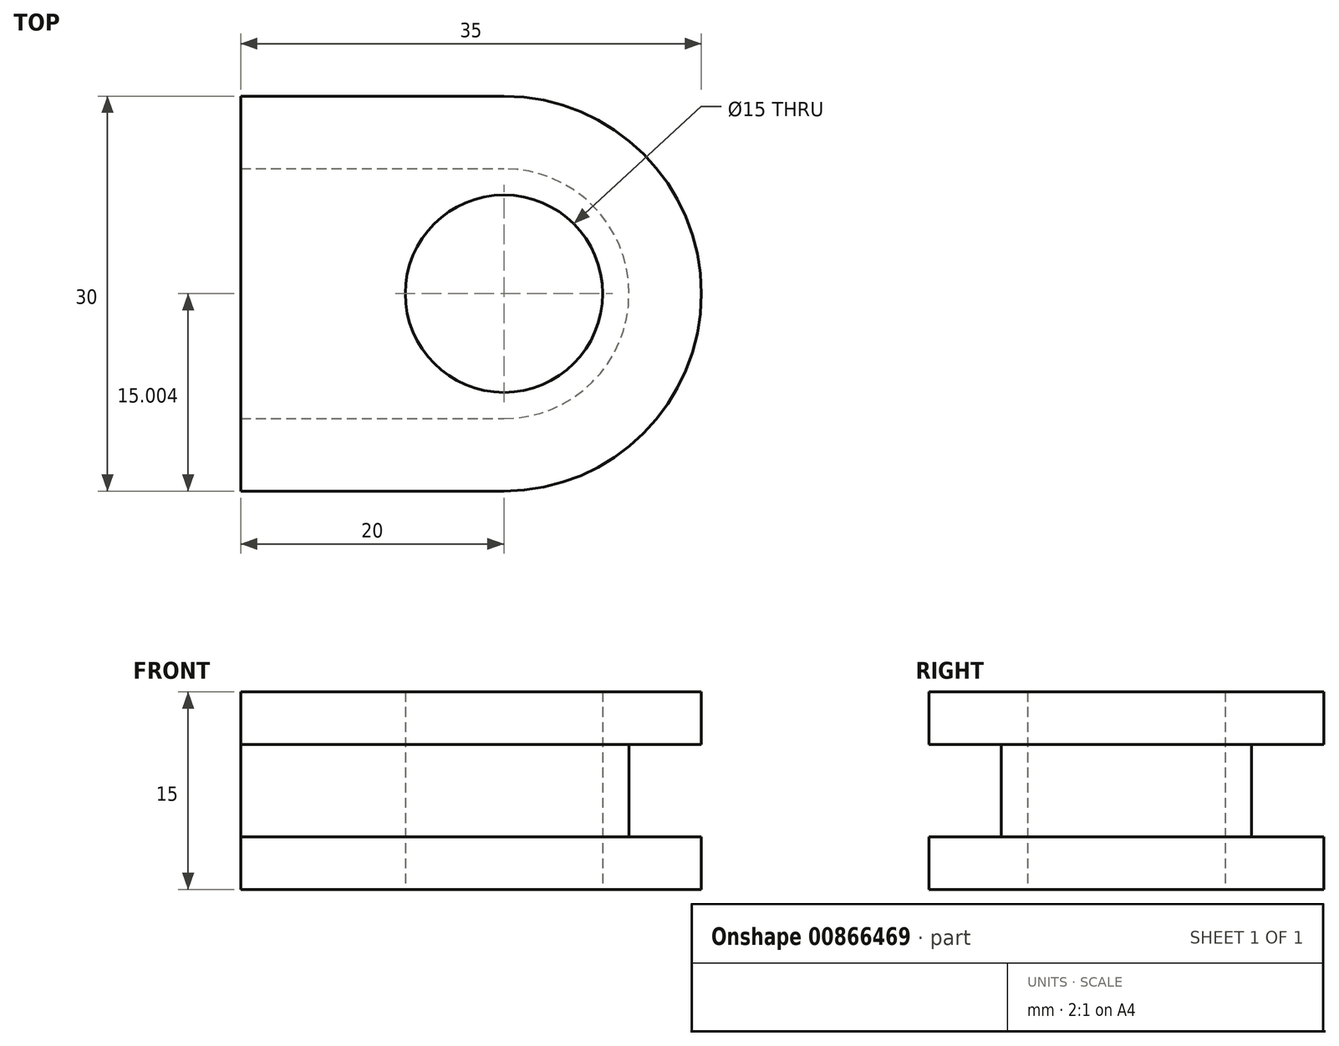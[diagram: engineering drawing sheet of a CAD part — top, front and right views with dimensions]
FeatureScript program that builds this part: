
annotation { "Feature Type Name" : "Feature", "Feature Type Description" : "" }
export const myFeature = defineFeature(function(context is Context, id is Id, definition is map)
    precondition{}
    {
        {
            var Q0;
            Q0=qCreatedBy(makeId("Top.planeOp"),FACE);
            var sketch = newSketch(context, id + "F0", { "sketchPlane" : qUnion([Q0])});
            skLineSegment(sketch, "E0", {"start": v(12.02, 13.64) * mm, "end": v(12.02, -16.36) * mm});
            skLineSegment(sketch, "E1", {"start": v(12.02, 13.64) * mm, "end": v(32.02, 13.64) * mm});
            skLineSegment(sketch, "E2", {"start": v(12.02, -16.36) * mm, "end": v(32.02, -16.36) * mm});
            skArc(sketch, "E3", {"start": v(32.02, 13.64) * mm, "mid": v(47.02, -1.36) * mm, "end": v(32.02, -16.36) * mm});
            skCircle(sketch, "E4", {"center": v(32.02, -1.36) * mm, "radius": 7.5 * mm});
            skArc(sketch, "E5", {"start": v(32.02, -10.86) * mm, "mid": v(41.52, -1.36) * mm, "end": v(32.02, 8.14) * mm});
            skLineSegment(sketch, "E6", {"start": v(12.02, 8.14) * mm, "end": v(32.02, 8.14) * mm});
            skLineSegment(sketch, "E7", {"start": v(12.02, -10.86) * mm, "end": v(32.02, -10.86) * mm});
            skSolve(sketch);
        }
        {
            var Q0;
            {var subQ0=sQuery(id+"F0.wireOp",EDGE,"E6");Q0=makeQuery(id+"F0.imprint","IMPRINT",FACE,{"disambiguationData":[TD([[makeQuery(id+"F0.imprint","IMPRINT",EDGE,{"derivedFrom":subQ0}),-1.0]])]});}
            var Q1;
            Q1=makeQuery(id+"F0.imprint","IMPRINT",FACE,{"disambiguationData":[TD([[makeQuery(id+"F0.imprint","IMPRINT",EDGE,{"derivedFrom":sQuery(id+"F0.wireOp",EDGE,"E4")}),-1.0]])]});
            var Q2;
            {var subQ1=sQuery(id+"F0.wireOp",EDGE,"E1");Q2=makeQuery(id+"F0.imprint","IMPRINT",FACE,{"disambiguationData":[TD([[makeQuery(id+"F0.imprint","IMPRINT",EDGE,{"derivedFrom":subQ1}),-1.0]])]});}
            extrude(context, id + "F1", {"entities" : qUnion([Q0, Q1, Q2]), "endBound" : BoundingType.SYMMETRIC, "depth" : 15 * mm, "offsetDistance" : 25 * mm});
        }
        {
            var Q0;
            {var subQ1=sQuery(id+"F0.wireOp",EDGE,"E1");Q0=makeQuery(id+"F0.imprint","IMPRINT",FACE,{"disambiguationData":[TD([[makeQuery(id+"F0.imprint","IMPRINT",EDGE,{"derivedFrom":subQ1}),-1.0]])]});}
            extrude(context, id + "F2", {"entities" : qUnion([Q0]), "operationType" : NewBodyOperationType.REMOVE, "endBound" : BoundingType.SYMMETRIC, "depth" : 7 * mm, "offsetDistance" : 25 * mm});
        }
    });
